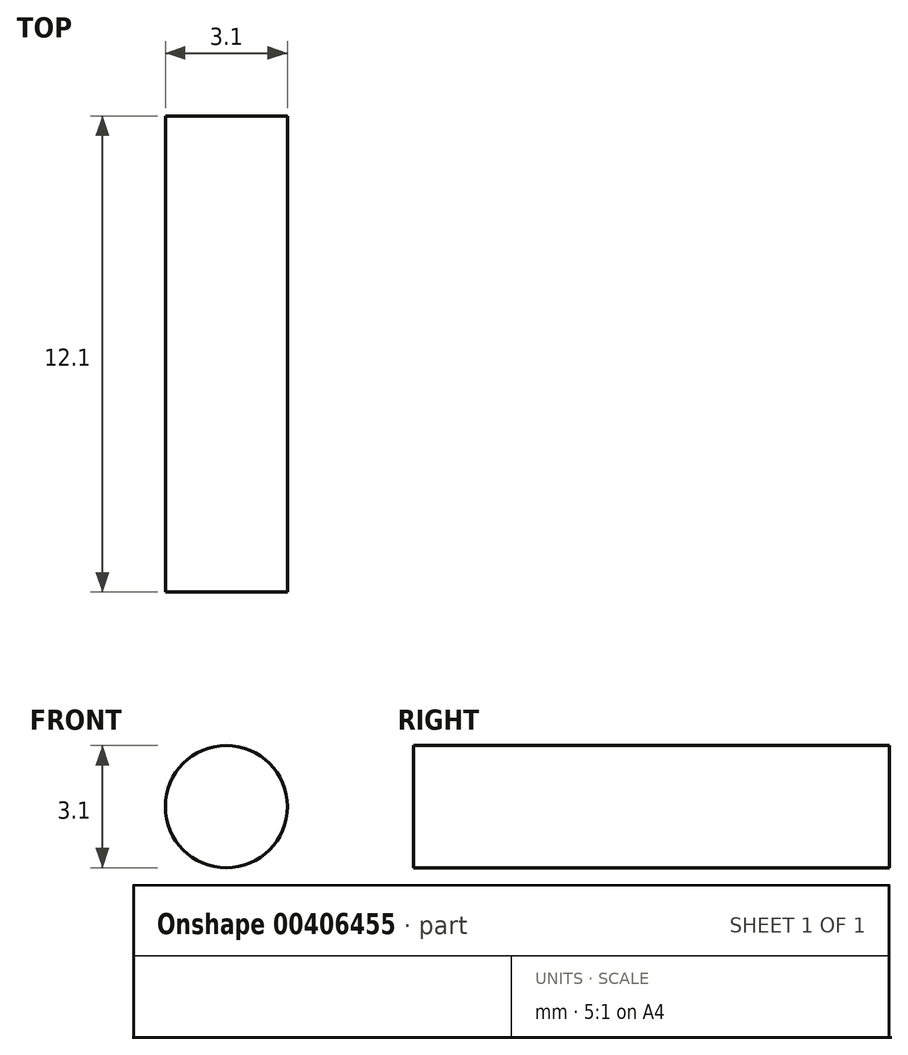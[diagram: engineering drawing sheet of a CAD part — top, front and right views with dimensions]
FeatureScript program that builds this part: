
annotation { "Feature Type Name" : "Feature", "Feature Type Description" : "" }
export const myFeature = defineFeature(function(context is Context, id is Id, definition is map)
    precondition{}
    {
        {
            var Q0;
            Q0=qCreatedBy(makeId("Front.planeOp"),FACE);
            var sketch = newSketch(context, id + "F0", { "sketchPlane" : qUnion([Q0])});
            skCircle(sketch, "E0", {"center": v(0, 0) * mm, "radius": 1.55 * mm});
            skSolve(sketch);
        }
        {
            var Q0;
            Q0 = qSketchRegion(id + "F0", true);
            extrude(context, id + "F1", {"entities" : qUnion([Q0]), "depth" : 12.1 * mm});
        }
    });
